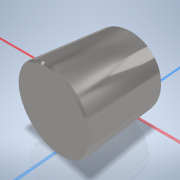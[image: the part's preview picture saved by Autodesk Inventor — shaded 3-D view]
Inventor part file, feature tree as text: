
AUTODESK INVENTOR PART (.ipt)
format: ipt  version: 2021 (Build 250183000, 183)  size: 114,176 bytes
history: native  units: mm
features: other x4, reference x2, extrude x1, chamfer x1, sketch x1
ambient origin geometry x8: Origin, YZ Plane, XZ Plane, XY Plane, X Axis, Y Axis, Z Axis, Center Point
bodies: Body1 (feature_tree)
feature tree (9):
  other  "Bryła1"
  extrude  "Wyciągnięcie proste1"  Depth=22.0mm
  chamfer  "Faza1"  Distance=17.0mm
  sketch  "Szkic1"
  reference  "Odniesienie1"
  reference  "Odniesienie2"
  parser-record x1  (decoder bookkeeping rows leaked as tree rows — omitted from the tree; the rows remain in map.json)
  other  "model tensometru.iam"
  other  "szklo:1"
note: 1 file-system path scrubbed to <path> (originals preserved in map.json)
